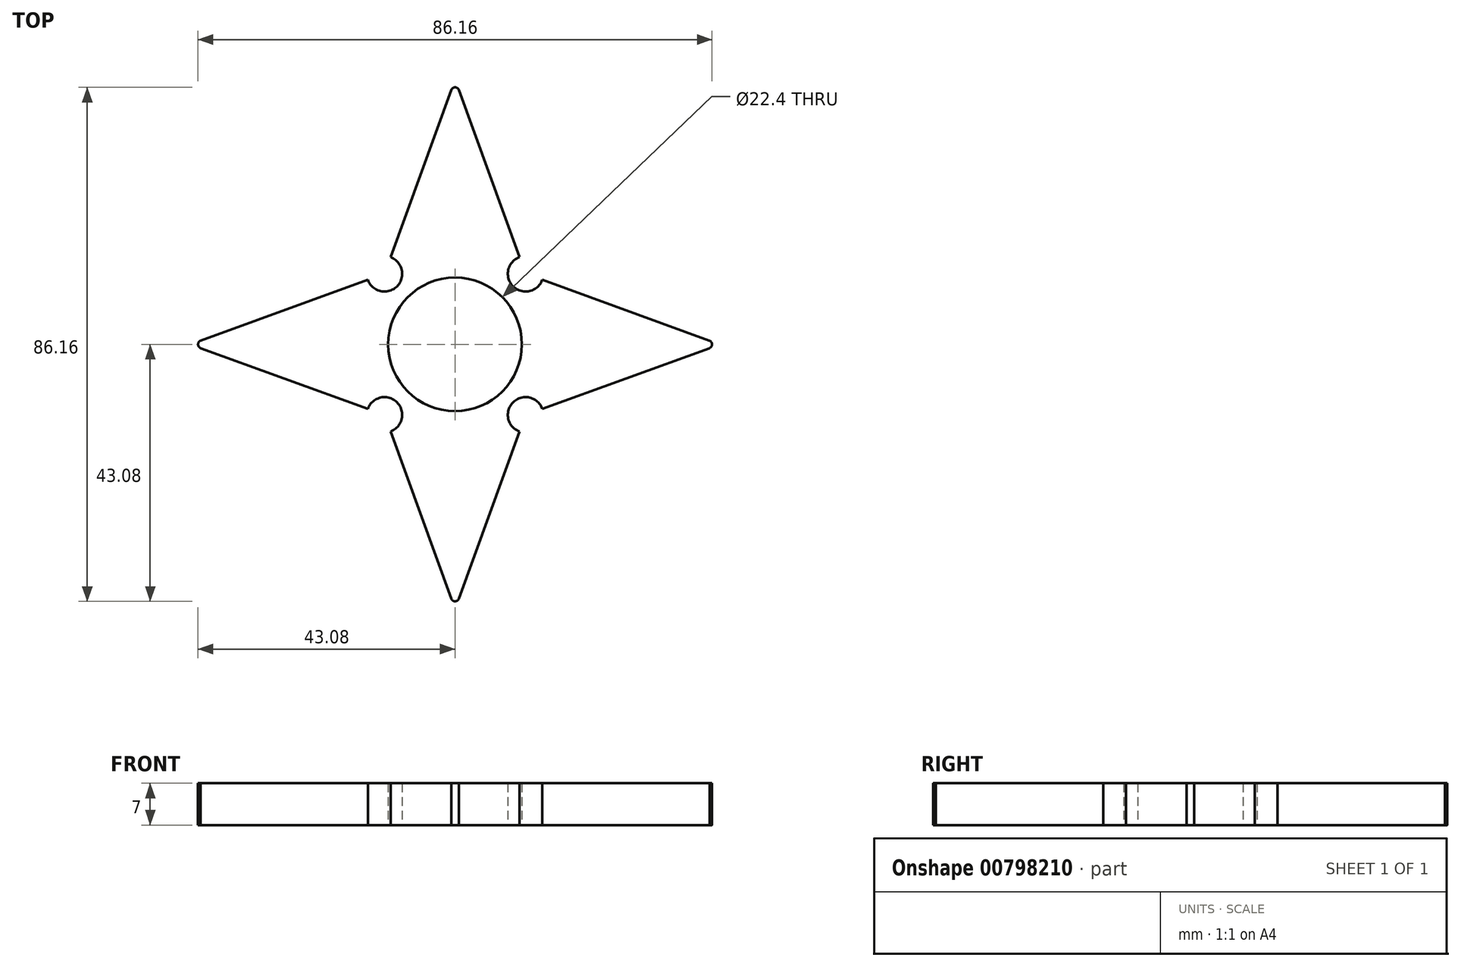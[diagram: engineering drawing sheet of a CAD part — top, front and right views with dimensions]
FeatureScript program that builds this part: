
annotation { "Feature Type Name" : "Feature", "Feature Type Description" : "" }
export const myFeature = defineFeature(function(context is Context, id is Id, definition is map)
    precondition{}
    {
        {
            var Q0;
            Q0=qCreatedBy(makeId("Top.planeOp"),FACE);
            var sketch = newSketch(context, id + "F0", { "sketchPlane" : qUnion([Q0])});
            skCircle(sketch, "E0", {"center": v(0, 0) * mm, "radius": 11.2 * mm});
            skLineSegment(sketch, "E1", {"start": v(-0.63, 42.65) * mm, "end": v(-10.81, 14.62) * mm});
            skLineSegment(sketch, "E2", {"start": v(-14.62, 10.81) * mm, "end": v(-42.66, 0.63) * mm});
            skLineSegment(sketch, "E3", {"start": v(-42.65, -0.63) * mm, "end": v(-14.62, -10.81) * mm});
            skLineSegment(sketch, "E4", {"start": v(-10.81, -14.62) * mm, "end": v(-0.63, -42.66) * mm});
            skLineSegment(sketch, "E5", {"start": v(0.63, -42.65) * mm, "end": v(10.81, -14.62) * mm});
            skLineSegment(sketch, "E6", {"start": v(14.62, -10.81) * mm, "end": v(42.66, -0.63) * mm});
            skLineSegment(sketch, "E7", {"start": v(42.65, 0.63) * mm, "end": v(14.62, 10.81) * mm});
            skLineSegment(sketch, "E8", {"start": v(10.81, 14.62) * mm, "end": v(0.63, 42.66) * mm});
            skArc(sketch, "E9", {"start": v(-14.62, 10.81) * mm, "mid": v(-9.72, 9.72) * mm, "end": v(-10.81, 14.62) * mm});
            skArc(sketch, "E10.1.0", {"start": v(-10.81, -14.62) * mm, "mid": v(-9.72, -9.72) * mm, "end": v(-14.62, -10.81) * mm});
            skArc(sketch, "E10.2.0", {"start": v(14.62, -10.81) * mm, "mid": v(9.72, -9.72) * mm, "end": v(10.81, -14.62) * mm});
            skArc(sketch, "E10.3.0", {"start": v(10.81, 14.62) * mm, "mid": v(9.72, 9.72) * mm, "end": v(14.62, 10.81) * mm});
            skPoint(sketch, "E11.orphan", {"position": v(-75, 75) * mm});
            skPoint(sketch, "E12.orphan", {"position": v(75, -75) * mm});
            skPoint(sketch, "E13.orphan", {"position": v(-75, -75) * mm});
            skPoint(sketch, "E14.orphan", {"position": v(75, 75) * mm});
            skPoint(sketch, "E15.end.orphan", {"position": v(0, 36.94) * mm});
            skArc(sketch, "E16", {"start": v(0.63, 42.66) * mm, "mid": v(-0.02, 43.08) * mm, "end": v(-0.64, 42.62) * mm});
            skPoint(sketch, "E17.orphan", {"position": v(0, 44.4) * mm});
            skArc(sketch, "E18.1.0", {"start": v(-42.66, 0.63) * mm, "mid": v(-43.08, -0.02) * mm, "end": v(-42.62, -0.64) * mm});
            skArc(sketch, "E18.2.0", {"start": v(-0.63, -42.66) * mm, "mid": v(0.02, -43.08) * mm, "end": v(0.64, -42.62) * mm});
            skArc(sketch, "E18.3.0", {"start": v(42.66, -0.63) * mm, "mid": v(43.08, 0.02) * mm, "end": v(42.62, 0.64) * mm});
            skPoint(sketch, "E19.orphan", {"position": v(-44.4, 0) * mm});
            skSolve(sketch);
        }
        {
            var Q0;
            Q0=makeQuery(id+"F0.imprint","IMPRINT",FACE,{"disambiguationData":[TD([[makeQuery(id+"F0.imprint","IMPRINT",EDGE,{"derivedFrom":sQuery(id+"F0.wireOp",EDGE,"E0")}),-1.0]])]});
            extrude(context, id + "F1", {"entities" : qUnion([Q0]), "depth" : 7 * mm, "offsetDistance" : 25 * mm});
        }
    });
